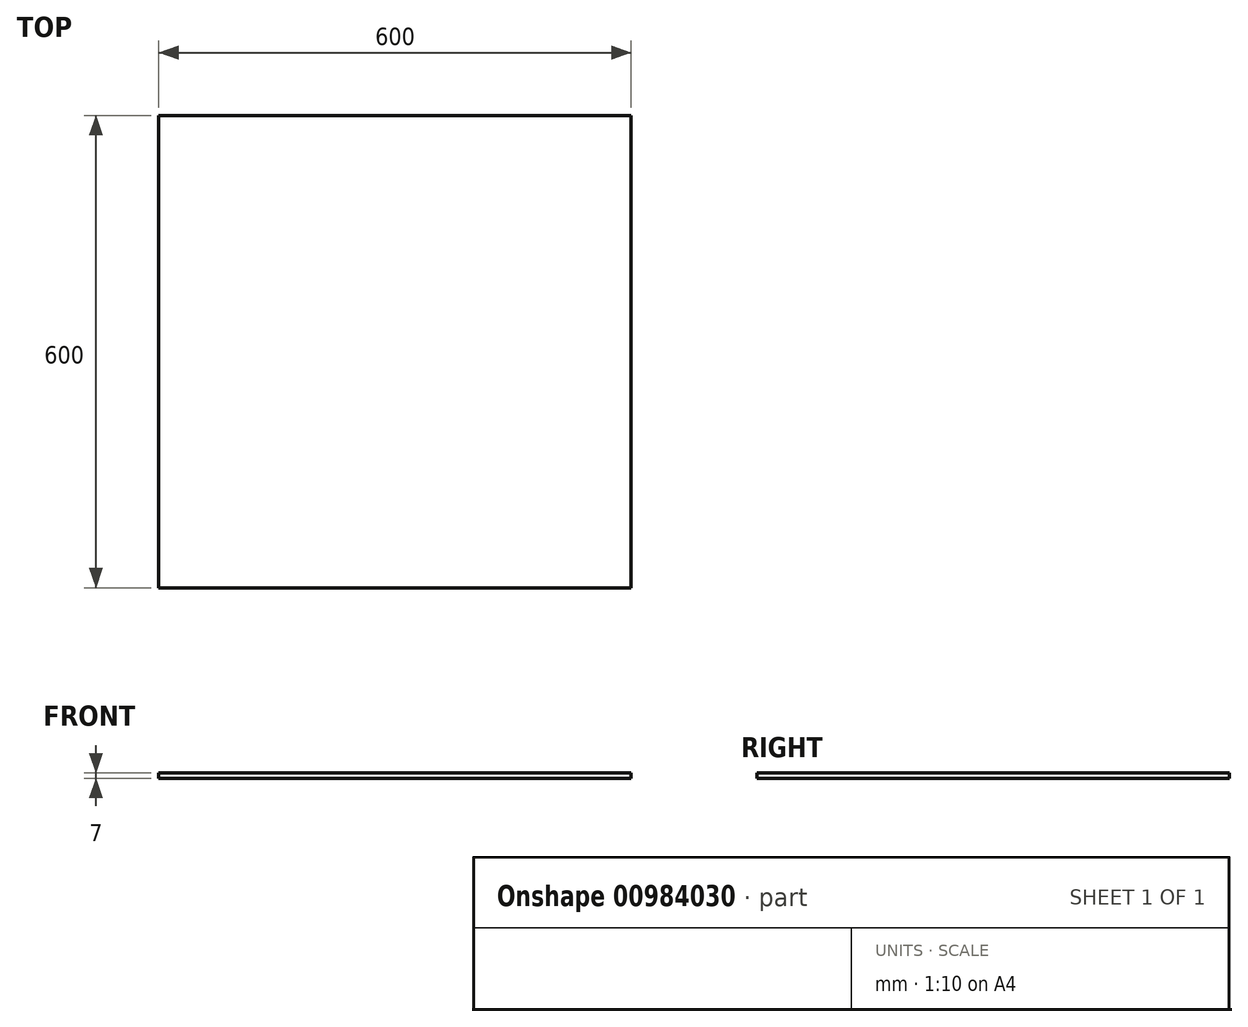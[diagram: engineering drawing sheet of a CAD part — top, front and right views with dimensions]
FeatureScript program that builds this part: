
annotation { "Feature Type Name" : "Feature", "Feature Type Description" : "" }
export const myFeature = defineFeature(function(context is Context, id is Id, definition is map)
    precondition{}
    {
        {
            var Q0;
            Q0=qCreatedBy(makeId("Top.planeOp"),FACE);
            var sketch = newSketch(context, id + "F0", { "sketchPlane" : qUnion([Q0])});
            skLineSegment(sketch, "E0.bottom", {"start": v(-300, 0) * mm, "end": v(300, 0) * mm});
            skLineSegment(sketch, "E0.top", {"start": v(-300, 600) * mm, "end": v(300, 600) * mm});
            skLineSegment(sketch, "E0.left", {"start": v(-300, 0) * mm, "end": v(-300, 600) * mm});
            skLineSegment(sketch, "E0.right", {"start": v(300, 0) * mm, "end": v(300, 600) * mm});
            skPoint(sketch, "E0.middle", {"position": v(0, 300) * mm});
            skSolve(sketch);
        }
        {
            var Q0;
            Q0=makeQuery(id+"F0.imprint","IMPRINT",FACE,{"disambiguationData":[TD([[makeQuery(id+"F0.imprint","IMPRINT",EDGE,{"derivedFrom":sQuery(id+"F0.wireOp",EDGE,"E0.bottom")}),1.0]])]});
            extrude(context, id + "F1", {"entities" : qUnion([Q0]), "oppositeDirection" : true, "depth" : 7 * mm, "offsetDistance" : 25 * mm});
        }
    });
